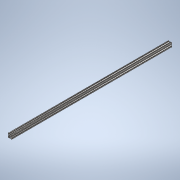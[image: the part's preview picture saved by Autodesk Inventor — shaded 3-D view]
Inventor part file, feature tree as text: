
AUTODESK INVENTOR PART (.ipt)
format: ipt  version: 2020 (Build 240168000, 168)  size: 247,296 bytes
history: native  units: in
note: dims shown in document units (in); Inventor stores cm internally (conversion verified against a paired STEP export)
features: extrude x1, sketch x1
ambient origin geometry x8: Origin, YZ Plane, XZ Plane, XY Plane, X Axis, Y Axis, Z Axis, Center Point
bodies: Solid1 (feature_tree)
feature tree (2):
  extrude  "Extrusion1"  [1 undecoded]
  sketch  "Sketch1"  dims[d0=40.0in d1=0.0in]
note: 1 required parameter value undecoded (feature->parameter linkage not recoverable at this tier; creation-order binding heuristic only, values carry confidence <= 0.55)
